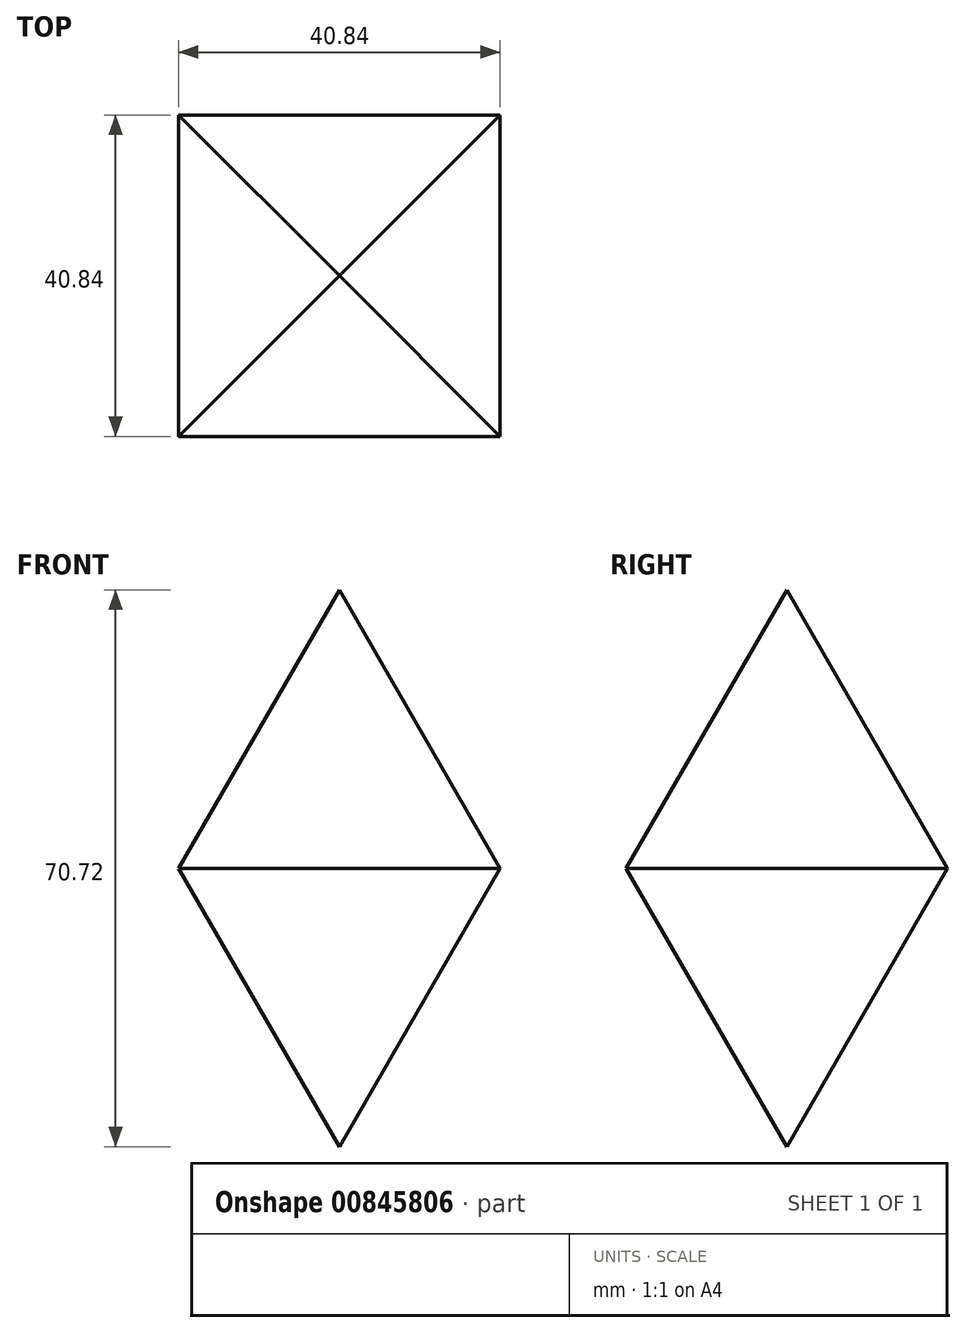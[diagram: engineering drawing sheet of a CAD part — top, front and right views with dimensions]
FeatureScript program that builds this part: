
annotation { "Feature Type Name" : "Feature", "Feature Type Description" : "" }
export const myFeature = defineFeature(function(context is Context, id is Id, definition is map)
    precondition{}
    {
        {
            var Q0;
            Q0=qCreatedBy(makeId("Top.planeOp"),FACE);
            var sketch = newSketch(context, id + "F0", { "sketchPlane" : qUnion([Q0])});
            skLineSegment(sketch, "E0.bottom", {"start": v(-20.42, -20.42) * mm, "end": v(20.42, -20.42) * mm});
            skLineSegment(sketch, "E0.top", {"start": v(-20.42, 20.42) * mm, "end": v(20.42, 20.42) * mm});
            skLineSegment(sketch, "E0.left", {"start": v(-20.42, -20.42) * mm, "end": v(-20.42, 20.42) * mm});
            skLineSegment(sketch, "E0.right", {"start": v(20.42, -20.42) * mm, "end": v(20.42, 20.42) * mm});
            skPoint(sketch, "E0.middle", {"position": v(0, 0) * mm});
            skSolve(sketch);
        }
        {
            var Q0;
            Q0=makeQuery(id+"F0.imprint","IMPRINT",FACE,{"disambiguationData":[TD([[makeQuery(id+"F0.imprint","IMPRINT",EDGE,{"derivedFrom":sQuery(id+"F0.wireOp",EDGE,"E0.bottom")}),1.0]])]});
            extrude(context, id + "F1", {"entities" : qUnion([Q0]), "depth" : 40.9 * mm, "offsetDistance" : 25.4 * mm, "hasDraft" : true, "draftAngle" : 30 * degree, "draftPullDirection" : true, "hasSecondDirection" : true, "secondDirectionOppositeDirection" : true, "secondDirectionDepth" : 40.9 * mm, "hasSecondDirectionDraft" : true, "secondDirectionDraftAngle" : 30 * degree, "secondDirectionDraftPullDirection" : true});
        }
    });
